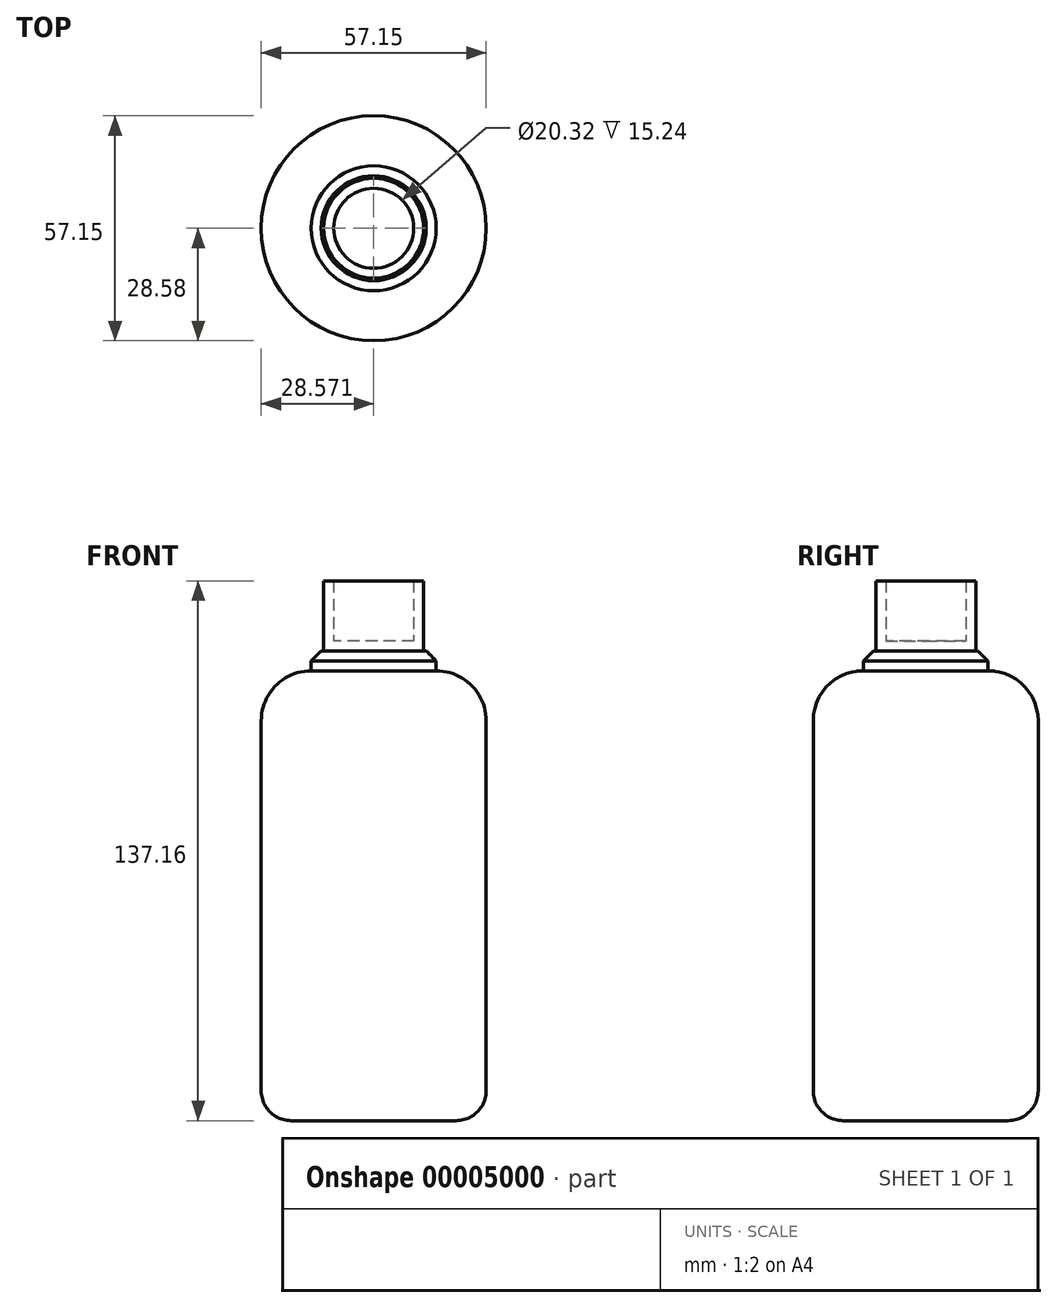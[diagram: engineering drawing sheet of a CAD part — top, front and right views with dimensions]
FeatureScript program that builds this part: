
annotation { "Feature Type Name" : "Feature", "Feature Type Description" : "" }
export const myFeature = defineFeature(function(context is Context, id is Id, definition is map)
    precondition{}
    {
        {
            var Q0;
            Q0=qCreatedBy(makeId("Top.planeOp"),FACE);
            var sketch = newSketch(context, id + "F0", { "sketchPlane" : qUnion([Q0])});
            skCircle(sketch, "E0", {"center": v(-0.39, 3.34) * mm, "radius": 28.58 * mm});
            skSolve(sketch);
        }
        {
            var Q0;
            Q0=makeQuery(id+"F0.imprint","IMPRINT",FACE,{"disambiguationData":[TD([[makeQuery(id+"F0.imprint","IMPRINT",EDGE,{"derivedFrom":sQuery(id+"F0.wireOp",EDGE,"E0")}),1.0]])]});
            extrude(context, id + "F1", {"entities" : qUnion([Q0]), "depth" : 101.6 * mm});
        }
        {
            var Q0;
            Q0=makeQuery(id+"F1.opExtrude","CAP_FACE",FACE,{"disambiguationData":[OSD([sQuery(id+"F0.wireOp",EDGE,"E0")])],"isStart":true});
            fillet(context, id + "F2", {"entities" : qUnion([Q0]), "radius" : 7.62 * mm, "tangentPropagation" : true, "allowEdgeOverflow" : false});
        }
        {
            var Q0;
            Q0=makeQuery(id+"F1.opExtrude","CAP_FACE",FACE,{"disambiguationData":[OSD([sQuery(id+"F0.wireOp",EDGE,"E0")])],"isStart":false});
            var sketch = newSketch(context, id + "F3", { "sketchPlane" : qUnion([Q0])});
            skCircle(sketch, "E1", {"center": v(-0.39, 3.34) * mm, "radius": 28.58 * mm});
            skSolve(sketch);
        }
        {
            var Q0;
            Q0=makeQuery(id+"F3.imprint","IMPRINT",FACE,{"disambiguationData":[TD([[makeQuery(id+"F3.imprint","IMPRINT",EDGE,{"derivedFrom":sQuery(id+"F3.wireOp",EDGE,"E1")}),1.0]])]});
            extrude(context, id + "F4", {"entities" : qUnion([Q0]), "operationType" : NewBodyOperationType.ADD, "depth" : 12.7 * mm});
        }
        {
            var Q0;
            Q0=makeQuery(id+"F4.opExtrude","CAP_FACE",FACE,{"disambiguationData":[OSD([sQuery(id+"F3.wireOp",EDGE,"E1")])],"isStart":false});
            fillet(context, id + "F5", {"entities" : qUnion([Q0]), "radius" : 12.7 * mm, "tangentPropagation" : true, "allowEdgeOverflow" : false});
        }
        {
            var Q0;
            Q0=makeQuery(id+"F4.opExtrude","CAP_FACE",FACE,{"disambiguationData":[OSD([sQuery(id+"F3.wireOp",EDGE,"E1")])],"isStart":false});
            var sketch = newSketch(context, id + "F6", { "sketchPlane" : qUnion([Q0])});
            skCircle(sketch, "E2", {"center": v(-0.39, 3.34) * mm, "radius": 15.87 * mm});
            skSolve(sketch);
        }
        {
            var Q0;
            Q0=makeQuery(id+"F6.imprint","IMPRINT",FACE,{"disambiguationData":[TD([[makeQuery(id+"F6.imprint","IMPRINT",EDGE,{"derivedFrom":sQuery(id+"F6.wireOp",EDGE,"E2")}),1.0]])]});
            extrude(context, id + "F7", {"entities" : qUnion([Q0]), "operationType" : NewBodyOperationType.ADD, "depth" : 5.08 * mm});
        }
        {
            var Q0;
            Q0=makeQuery(id+"F7.opExtrude","CAP_FACE",FACE,{"disambiguationData":[OSD([sQuery(id+"F6.wireOp",EDGE,"E2")])],"isStart":false});
            var sketch = newSketch(context, id + "F8", { "sketchPlane" : qUnion([Q0])});
            skCircle(sketch, "E3", {"center": v(-0.39, 3.34) * mm, "radius": 12.7 * mm});
            skSolve(sketch);
        }
        {
            var Q0;
            Q0=makeQuery(id+"F8.imprint","IMPRINT",FACE,{"disambiguationData":[TD([[makeQuery(id+"F8.imprint","IMPRINT",EDGE,{"derivedFrom":sQuery(id+"F8.wireOp",EDGE,"E3")}),1.0]])]});
            extrude(context, id + "F9", {"entities" : qUnion([Q0]), "depth" : 17.78 * mm});
        }
        {
            var Q0;
            Q0=makeQuery(id+"F7.opExtrude","CAP_FACE",FACE,{"disambiguationData":[OSD([sQuery(id+"F6.wireOp",EDGE,"E2")])],"isStart":false});
            chamfer(context, id + "F10", {"entities" : qUnion([Q0]), "width" : 2.54 * mm, "tangentPropagation" : true});
        }
        {
            var Q0;
            Q0=makeQuery(id+"F9.opExtrude","CAP_FACE",FACE,{"disambiguationData":[OSD([sQuery(id+"F8.wireOp",EDGE,"E3")])],"isStart":false});
            shell(context, id + "F11", {"entities" : qUnion([Q0]), "thickness" : 2.54 * mm});
        }
    });
